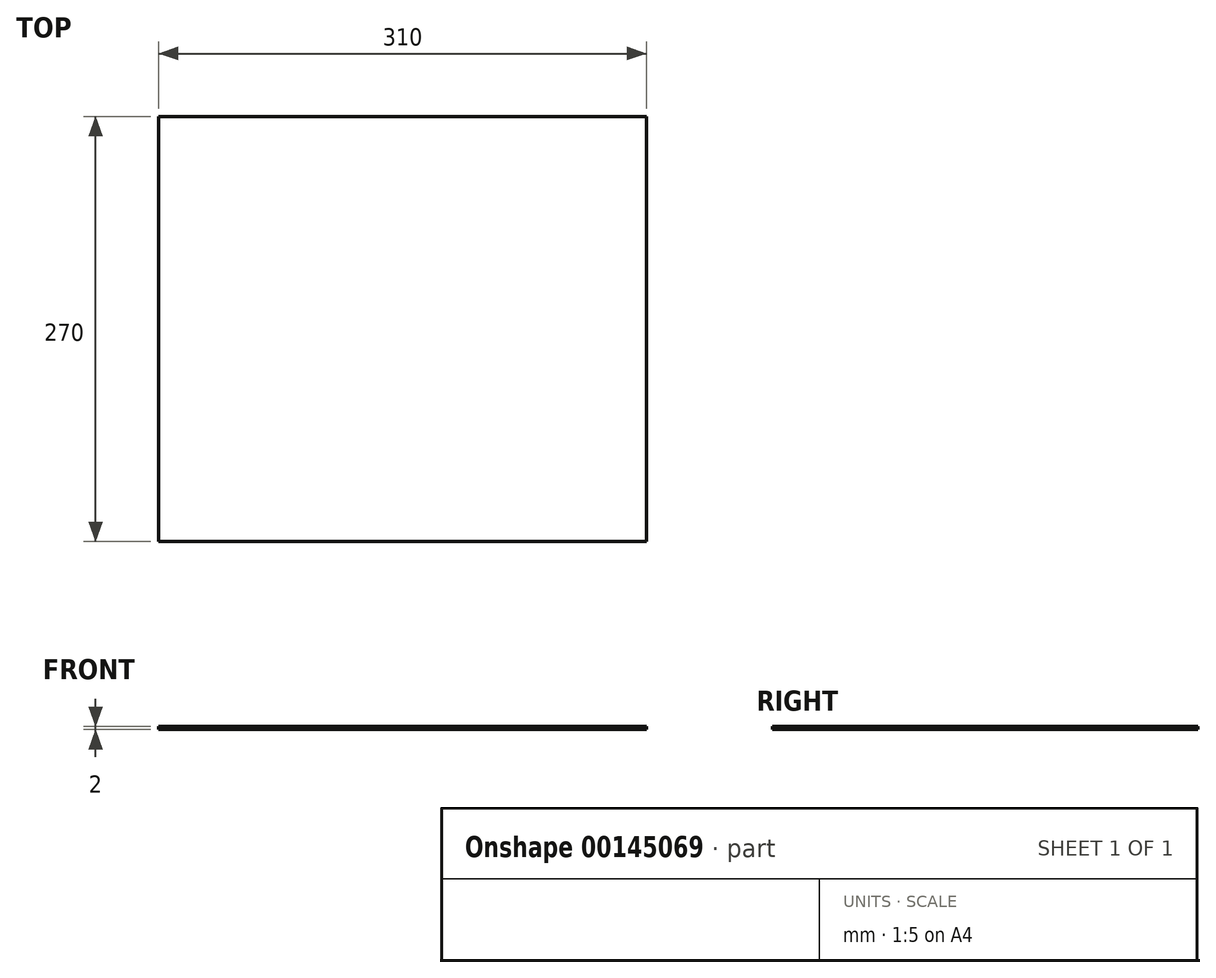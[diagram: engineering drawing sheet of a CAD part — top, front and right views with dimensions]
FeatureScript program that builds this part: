
annotation { "Feature Type Name" : "Feature", "Feature Type Description" : "" }
export const myFeature = defineFeature(function(context is Context, id is Id, definition is map)
    precondition{}
    {
        {
            var Q0;
            Q0=qCreatedBy(makeId("Top.planeOp"),FACE);
            var sketch = newSketch(context, id + "F0", { "sketchPlane" : qUnion([Q0])});
            skLineSegment(sketch, "E0.bottom", {"start": v(0, 0) * mm, "end": v(310, 0) * mm});
            skLineSegment(sketch, "E0.top", {"start": v(0, 270) * mm, "end": v(310, 270) * mm});
            skLineSegment(sketch, "E0.left", {"start": v(0, 0) * mm, "end": v(0, 270) * mm});
            skLineSegment(sketch, "E0.right", {"start": v(310, 0) * mm, "end": v(310, 270) * mm});
            skSolve(sketch);
        }
        {
            var Q0;
            Q0 = qSketchRegion(id + "F0", true);
            extrude(context, id + "F1", {"entities" : qUnion([Q0]), "depth" : 2 * mm});
        }
    });
